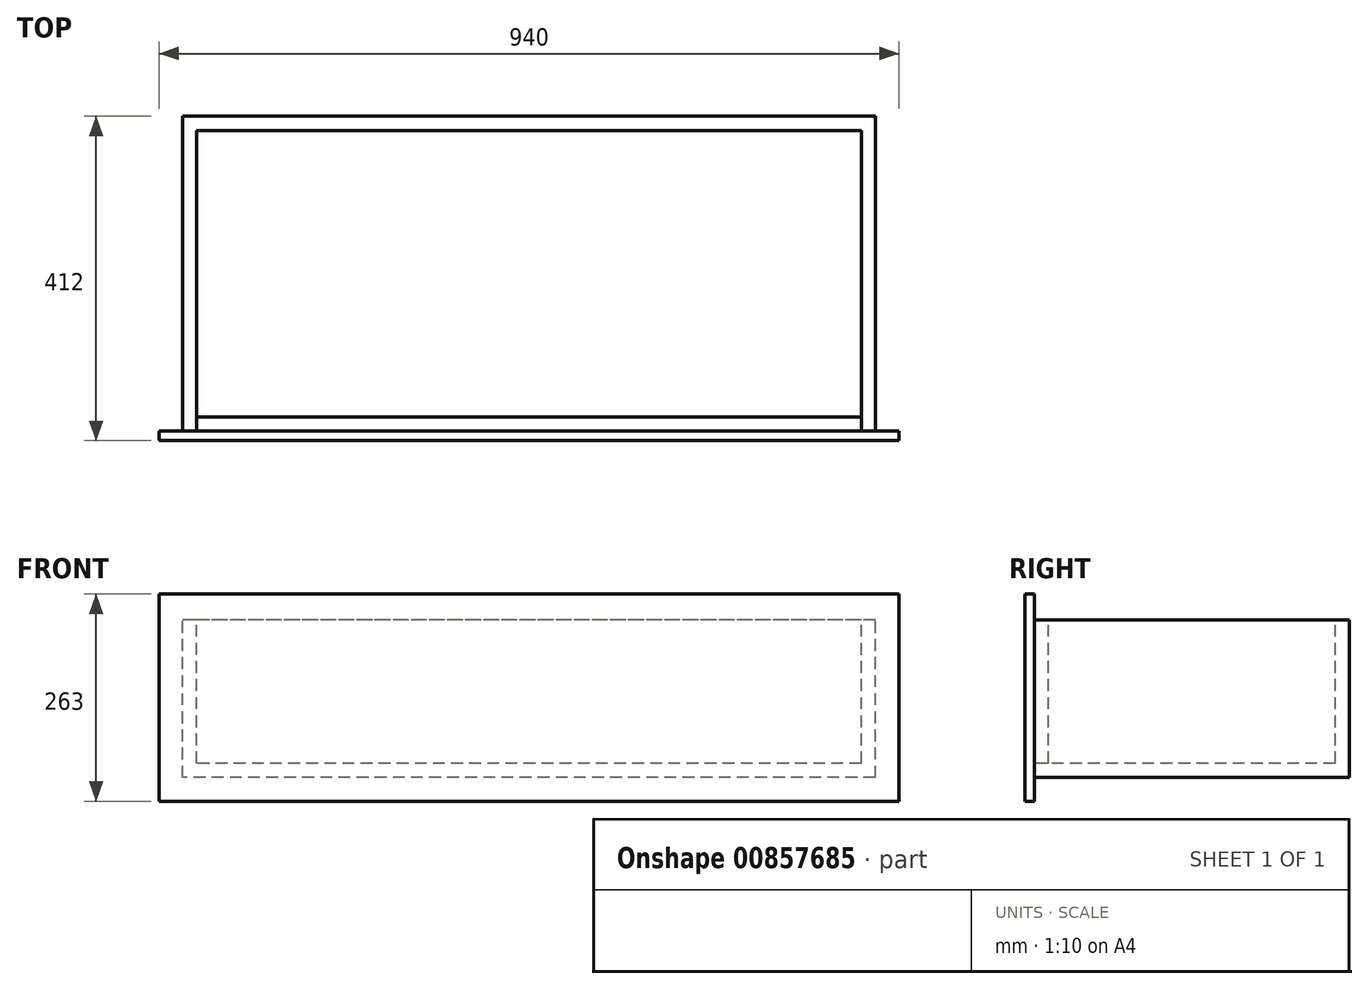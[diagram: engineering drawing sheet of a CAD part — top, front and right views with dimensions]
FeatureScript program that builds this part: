
annotation { "Feature Type Name" : "Feature", "Feature Type Description" : "" }
export const myFeature = defineFeature(function(context is Context, id is Id, definition is map)
    precondition{}
    {
        {
            var Q0;
            Q0=qCreatedBy(makeId("Front.planeOp"),FACE);
            var sketch = newSketch(context, id + "F0", { "sketchPlane" : qUnion([Q0])});
            skLineSegment(sketch, "E0.bottom", {"start": v(470, -131.5) * mm, "end": v(-470, -131.5) * mm});
            skLineSegment(sketch, "E0.top", {"start": v(470, 131.5) * mm, "end": v(-470, 131.5) * mm});
            skLineSegment(sketch, "E0.left", {"start": v(470, -131.5) * mm, "end": v(470, 131.5) * mm});
            skLineSegment(sketch, "E0.right", {"start": v(-470, -131.5) * mm, "end": v(-470, 131.5) * mm});
            skPoint(sketch, "E0.middle", {"position": v(0, 0) * mm});
            skLineSegment(sketch, "E1.bottom", {"start": v(440, -101.5) * mm, "end": v(-440, -101.5) * mm});
            skLineSegment(sketch, "E1.top", {"start": v(440, 98.5) * mm, "end": v(-440, 98.5) * mm});
            skLineSegment(sketch, "E1.left", {"start": v(440, -101.5) * mm, "end": v(440, 98.5) * mm});
            skLineSegment(sketch, "E1.right", {"start": v(-440, -101.5) * mm, "end": v(-440, 98.5) * mm});
            skLineSegment(sketch, "E2.0", {"start": v(422, -83.5) * mm, "end": v(422, 98.5) * mm});
            skLineSegment(sketch, "E3.0", {"start": v(-422, -83.5) * mm, "end": v(-422, 98.5) * mm});
            skLineSegment(sketch, "E4.0", {"start": v(404, -83.5) * mm, "end": v(-440, -83.5) * mm});
            skLineSegment(sketch, "E5", {"start": v(404, -83.5) * mm, "end": v(422, -83.5) * mm});
            skSolve(sketch);
        }
        {
            var Q0;
            {var subQ3=sQuery(id+"F0.wireOp",EDGE,"E3.0");Q0=makeQuery(id+"F0.imprint","IMPRINT",FACE,{"disambiguationData":[TD([[makeQuery(id+"F0.imprint","IMPRINT",EDGE,{"derivedFrom":subQ3}),1.0]])]});}
            var Q1;
            {var subQ1=sQuery(id+"F0.wireOp",EDGE,"E1.bottom");Q1=makeQuery(id+"F0.imprint","IMPRINT",FACE,{"disambiguationData":[TD([[makeQuery(id+"F0.imprint","IMPRINT",EDGE,{"derivedFrom":subQ1}),-1.0]])]});}
            var Q2;
            {var subQ3=sQuery(id+"F0.wireOp",EDGE,"E2.0");Q2=makeQuery(id+"F0.imprint","IMPRINT",FACE,{"disambiguationData":[TD([[makeQuery(id+"F0.imprint","IMPRINT",EDGE,{"derivedFrom":subQ3}),-1.0]])]});}
            extrude(context, id + "F1", {"entities" : qUnion([Q0, Q1, Q2]), "oppositeDirection" : true, "depth" : 400 * mm, "offsetDistance" : 25 * mm});
        }
        {
            var Q0;
            {var subQ0=sQuery(id+"F0.wireOp",EDGE,"E2.0");Q0=makeQuery(id+"F0.imprint","IMPRINT",FACE,{"disambiguationData":[TD([[makeQuery(id+"F0.imprint","IMPRINT",EDGE,{"derivedFrom":subQ0}),1.0]])]});}
            var Q1;
            {var subQ1=sQuery(id+"F0.wireOp",EDGE,"E1.bottom");Q1=makeQuery(id+"F0.imprint","IMPRINT",FACE,{"disambiguationData":[TD([[makeQuery(id+"F0.imprint","IMPRINT",EDGE,{"derivedFrom":subQ1}),-1.0]])]});}
            var Q2;
            Q2=makeQuery(id+"F0.imprint","IMPRINT",FACE,{"disambiguationData":[TD([[makeQuery(id+"F0.imprint","IMPRINT",EDGE,{"derivedFrom":sQuery(id+"F0.wireOp",EDGE,"E0.bottom")}),-1.0]])]});
            var Q3;
            {var subQ3=sQuery(id+"F0.wireOp",EDGE,"E2.0");Q3=makeQuery(id+"F0.imprint","IMPRINT",FACE,{"disambiguationData":[TD([[makeQuery(id+"F0.imprint","IMPRINT",EDGE,{"derivedFrom":subQ3}),-1.0]])]});}
            var Q4;
            {var subQ3=sQuery(id+"F0.wireOp",EDGE,"E3.0");Q4=makeQuery(id+"F0.imprint","IMPRINT",FACE,{"disambiguationData":[TD([[makeQuery(id+"F0.imprint","IMPRINT",EDGE,{"derivedFrom":subQ3}),1.0]])]});}
            extrude(context, id + "F2", {"entities" : qUnion([Q0, Q1, Q2, Q3, Q4]), "depth" : 12 * mm, "offsetDistance" : 25 * mm});
        }
        {
            var Q0;
            {var subQ3=sQuery(id+"F0.wireOp",EDGE,"E2.0");Q0=makeQuery(id+"F0.imprint","IMPRINT",FACE,{"disambiguationData":[TD([[makeQuery(id+"F0.imprint","IMPRINT",EDGE,{"derivedFrom":subQ3}),1.0]])]});}
            extrude(context, id + "F3", {"entities" : qUnion([Q0]), "oppositeDirection" : true, "depth" : 18 * mm, "offsetDistance" : 25 * mm});
        }
        {
            var Q0;
            Q0=makeQuery(id+"F1.opExtrude","CAP_FACE",FACE,{"disambiguationData":[OSD([sQuery(id+"F0.wireOp",EDGE,"E1.bottom"),sQuery(id+"F0.wireOp",EDGE,"E1.top"),sQuery(id+"F0.wireOp",EDGE,"E1.left"),sQuery(id+"F0.wireOp",EDGE,"E1.right"),sQuery(id+"F0.wireOp",EDGE,"E2.0"),sQuery(id+"F0.wireOp",EDGE,"E3.0"),sQuery(id+"F0.wireOp",EDGE,"E4.0"),sQuery(id+"F0.wireOp",EDGE,"E5")])],"isStart":false});
            var sketch = newSketch(context, id + "F4", { "sketchPlane" : qUnion([Q0])});
            skLineSegment(sketch, "E6.bottom", {"start": v(-422, 98.5) * mm, "end": v(422, 98.5) * mm});
            skLineSegment(sketch, "E6.top", {"start": v(-422, -83.5) * mm, "end": v(422, -83.5) * mm});
            skLineSegment(sketch, "E6.left", {"start": v(-422, 98.5) * mm, "end": v(-422, -83.5) * mm});
            skLineSegment(sketch, "E6.right", {"start": v(422, 98.5) * mm, "end": v(422, -83.5) * mm});
            skSolve(sketch);
        }
        {
            var Q0;
            Q0=makeQuery(id+"F4.imprint","IMPRINT",FACE,{"disambiguationData":[TD([[makeQuery(id+"F4.imprint","IMPRINT",EDGE,{"derivedFrom":sQuery(id+"F4.wireOp",EDGE,"E6.bottom")}),-1.0]])]});
            extrude(context, id + "F5", {"entities" : qUnion([Q0]), "operationType" : NewBodyOperationType.ADD, "oppositeDirection" : true, "depth" : 18 * mm, "offsetDistance" : 25 * mm});
        }
    });
